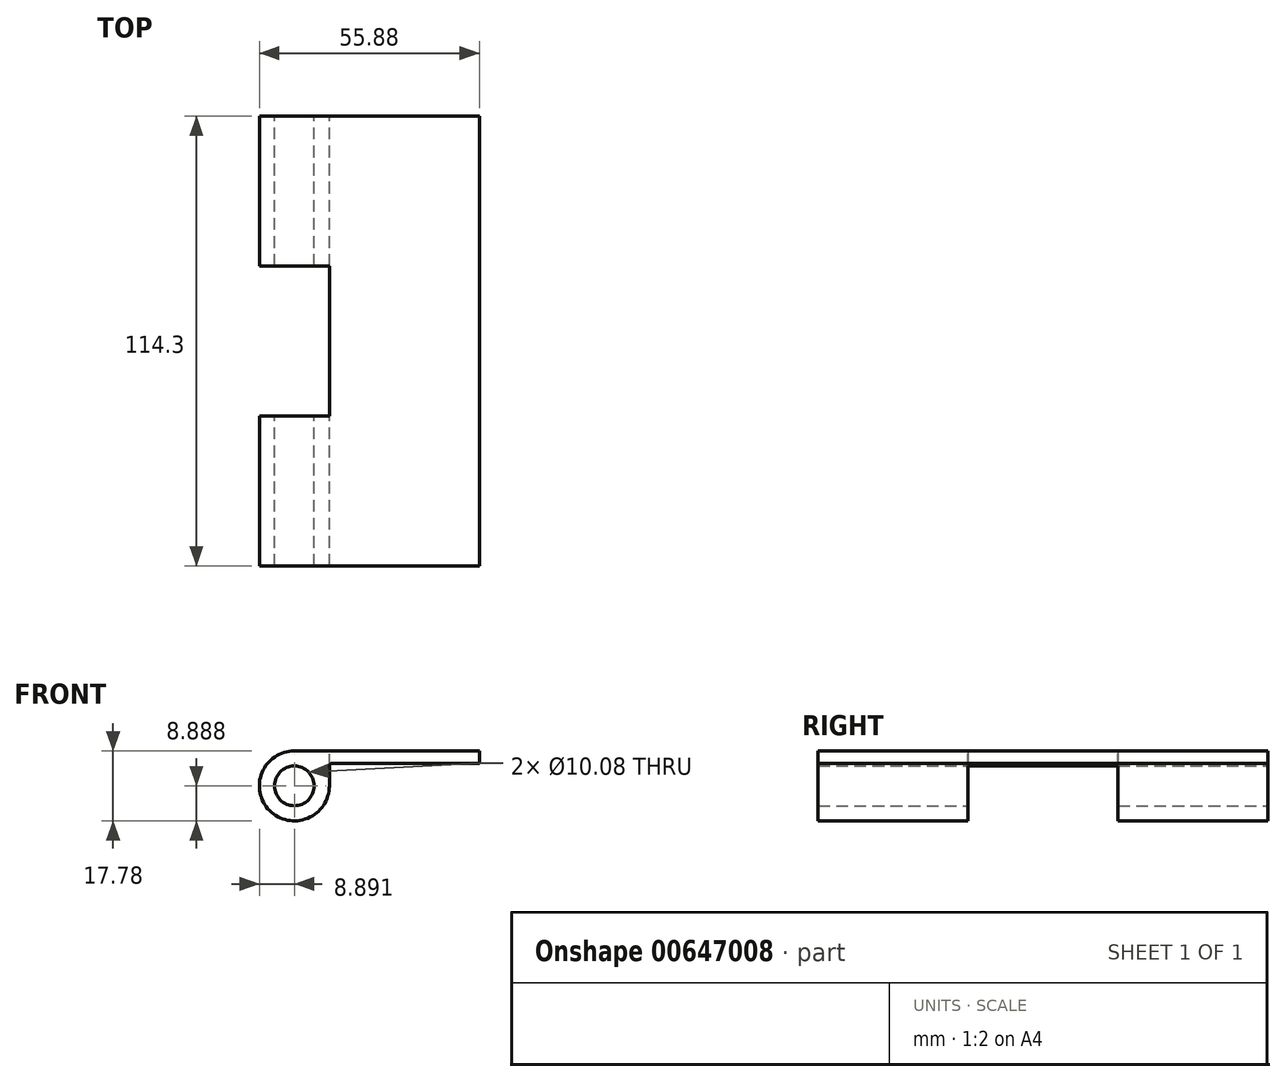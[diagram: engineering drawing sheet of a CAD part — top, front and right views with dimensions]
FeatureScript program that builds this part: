
annotation { "Feature Type Name" : "Feature", "Feature Type Description" : "" }
export const myFeature = defineFeature(function(context is Context, id is Id, definition is map)
    precondition{}
    {
        {
            var Q0;
            Q0=qCreatedBy(makeId("Front.planeOp"),FACE);
            var sketch = newSketch(context, id + "F0", { "sketchPlane" : qUnion([Q0])});
            skLineSegment(sketch, "E0", {"start": v(8.73, 0) * mm, "end": v(8.73, 1.57) * mm});
            skLineSegment(sketch, "E1", {"start": v(46.83, 5.38) * mm, "end": v(46.83, 2.2) * mm});
            skLineSegment(sketch, "E2", {"start": v(46.83, 2.2) * mm, "end": v(9.37, 2.2) * mm});
            skPoint(sketch, "E3.visualSharp", {"position": v(8.73, 2.2) * mm});
            skArc(sketch, "E3.filletArc", {"start": v(9.37, 2.2) * mm, "mid": v(8.92, 2.02) * mm, "end": v(8.73, 1.57) * mm});
            skCircle(sketch, "E4", {"center": v(-0.16, -3.51) * mm, "radius": 5.04 * mm});
            skArc(sketch, "E5", {"start": v(-0.16, 5.38) * mm, "mid": v(-6.44, -9.8) * mm, "end": v(8.73, -3.51) * mm});
            skLineSegment(sketch, "E6", {"start": v(46.83, 5.38) * mm, "end": v(-0.16, 5.38) * mm});
            skLineSegment(sketch, "E7", {"start": v(8.73, 0) * mm, "end": v(8.73, -3.51) * mm});
            skSolve(sketch);
        }
        {
            var Q0;
            Q0 = qSketchRegion(id + "F0", true);
            extrude(context, id + "F1", {"entities" : qUnion([Q0]), "depth" : 114.3 * mm, "offsetDistance" : 25.4 * mm});
        }
        {
            var Q0;
            Q0=makeQuery(id+"F1.opExtrude","SWEPT_FACE",FACE,{"disambiguationData":[OSD([sQuery(id+"F0.wireOp",EDGE,"E6")])]});
            var sketch = newSketch(context, id + "F2", { "sketchPlane" : qUnion([Q0])});
            skLineSegment(sketch, "E8.bottom", {"start": v(-9.05, -38.1) * mm, "end": v(8.73, -38.1) * mm});
            skLineSegment(sketch, "E8.top", {"start": v(-9.05, -76.2) * mm, "end": v(8.73, -76.2) * mm});
            skLineSegment(sketch, "E8.left", {"start": v(-9.05, -38.1) * mm, "end": v(-9.05, -76.2) * mm});
            skLineSegment(sketch, "E8.right", {"start": v(8.73, -38.1) * mm, "end": v(8.73, -76.2) * mm});
            skPoint(sketch, "E8.middle", {"position": v(-0.16, -57.15) * mm});
            skSolve(sketch);
        }
        {
            var Q0;
            Q0 = qSketchRegion(id + "F2", true);
            extrude(context, id + "F3", {"entities" : qUnion([Q0]), "operationType" : NewBodyOperationType.REMOVE, "oppositeDirection" : true, "depth" : 25.4 * mm, "offsetDistance" : 25.4 * mm});
        }
    });
